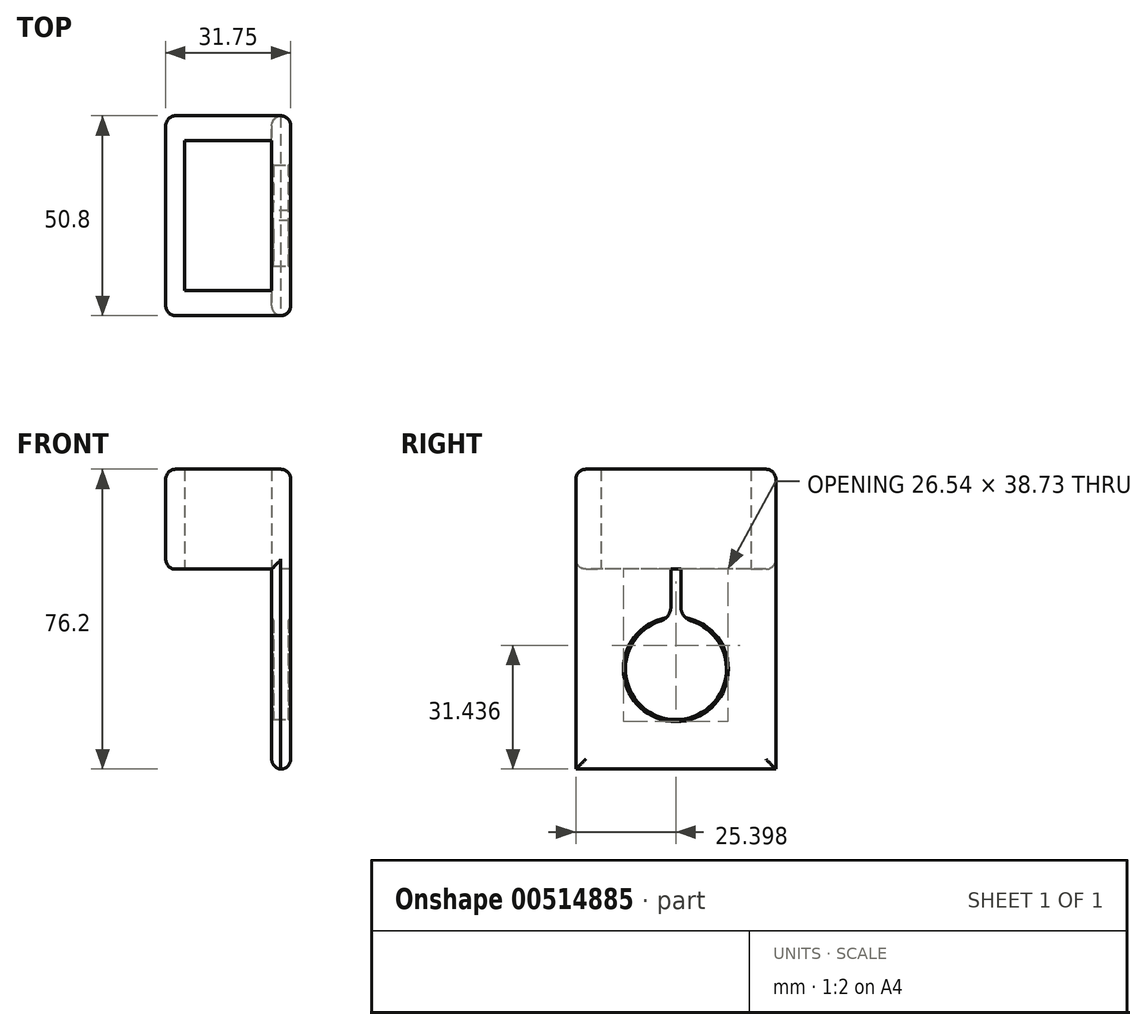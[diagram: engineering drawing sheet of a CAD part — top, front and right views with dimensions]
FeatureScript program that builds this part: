
annotation { "Feature Type Name" : "Feature", "Feature Type Description" : "" }
export const myFeature = defineFeature(function(context is Context, id is Id, definition is map)
    precondition{}
    {
        {
            var Q0;
            Q0=qCreatedBy(makeId("Top.planeOp"),FACE);
            var sketch = newSketch(context, id + "F0", { "sketchPlane" : qUnion([Q0])});
            skLineSegment(sketch, "E0.bottom", {"start": v(0, 0) * mm, "end": v(31.75, 0) * mm});
            skLineSegment(sketch, "E0.top", {"start": v(0, -50.8) * mm, "end": v(31.75, -50.8) * mm});
            skLineSegment(sketch, "E0.left", {"start": v(0, 0) * mm, "end": v(0, -50.8) * mm});
            skLineSegment(sketch, "E0.right", {"start": v(31.75, 0) * mm, "end": v(31.75, -50.8) * mm});
            skLineSegment(sketch, "E1.bottom", {"start": v(4.83, -6.35) * mm, "end": v(26.92, -6.35) * mm});
            skLineSegment(sketch, "E1.top", {"start": v(4.83, -44.45) * mm, "end": v(26.92, -44.45) * mm});
            skLineSegment(sketch, "E1.left", {"start": v(4.83, -6.35) * mm, "end": v(4.83, -44.45) * mm});
            skLineSegment(sketch, "E1.right", {"start": v(26.92, -6.35) * mm, "end": v(26.92, -44.45) * mm});
            skSolve(sketch);
        }
        {
            var Q0;
            Q0=makeQuery(id+"F0.imprint","IMPRINT",FACE,{"disambiguationData":[TD([[makeQuery(id+"F0.imprint","IMPRINT",EDGE,{"derivedFrom":sQuery(id+"F0.wireOp",EDGE,"E0.bottom")}),-1.0]])]});
            extrude(context, id + "F1", {"entities" : qUnion([Q0]), "depth" : 25.4 * mm, "offsetDistance" : 25.4 * mm});
        }
        {
            var Q0;
            Q0=makeQuery(id+"F1.opExtrude","CAP_FACE",FACE,{"disambiguationData":[OSD([sQuery(id+"F0.wireOp",EDGE,"E0.bottom"),sQuery(id+"F0.wireOp",EDGE,"E0.top"),sQuery(id+"F0.wireOp",EDGE,"E0.left"),sQuery(id+"F0.wireOp",EDGE,"E0.right"),sQuery(id+"F0.wireOp",EDGE,"E1.bottom"),sQuery(id+"F0.wireOp",EDGE,"E1.top"),sQuery(id+"F0.wireOp",EDGE,"E1.left"),sQuery(id+"F0.wireOp",EDGE,"E1.right")])],"isStart":true});
            var sketch = newSketch(context, id + "F2", { "sketchPlane" : qUnion([Q0])});
            skPoint(sketch, "E2", {"position": v(26.92, 5.08) * mm});
            skPoint(sketch, "E3", {"position": v(26.92, 6.35) * mm});
            skLineSegment(sketch, "E4", {"start": v(26.92, 5.08) * mm, "end": v(26.92, 6.35) * mm});
            skPoint(sketch, "E5", {"position": v(26.92, 45.72) * mm});
            skLineSegment(sketch, "E6", {"start": v(26.92, 44.45) * mm, "end": v(26.92, 45.72) * mm});
            skLineSegment(sketch, "E7.bottom", {"start": v(26.92, 5.08) * mm, "end": v(31.75, 5.08) * mm});
            skLineSegment(sketch, "E7.left", {"start": v(26.92, 5.08) * mm, "end": v(26.92, 45.72) * mm});
            skLineSegment(sketch, "E7.right", {"start": v(31.75, 5.08) * mm, "end": v(31.75, 45.72) * mm});
            skLineSegment(sketch, "E8", {"start": v(26.92, 5.08) * mm, "end": v(26.92, 0) * mm});
            skLineSegment(sketch, "E9", {"start": v(26.92, 0) * mm, "end": v(31.75, 0) * mm});
            skLineSegment(sketch, "E10", {"start": v(31.75, 0) * mm, "end": v(31.75, 5.08) * mm});
            skLineSegment(sketch, "E11", {"start": v(31.75, 45.72) * mm, "end": v(31.75, 50.8) * mm});
            skLineSegment(sketch, "E12", {"start": v(31.75, 50.8) * mm, "end": v(26.92, 50.8) * mm});
            skLineSegment(sketch, "E13", {"start": v(26.92, 50.8) * mm, "end": v(26.92, 45.72) * mm});
            skSolve(sketch);
        }
        {
            var Q0;
            Q0 = qSketchRegion(id + "F2", true);
            extrude(context, id + "F3", {"entities" : qUnion([Q0]), "operationType" : NewBodyOperationType.ADD, "depth" : 50.8 * mm, "offsetDistance" : 25.4 * mm});
        }
        {
            var Q0;
            Q0=makeQuery(id+"F3.boolean.opBoolean","MERGE",FACE,{"derivedFrom":[makeQuery(id+"F1.opExtrude","SWEPT_FACE",FACE,{"disambiguationData":[OSD([sQuery(id+"F0.wireOp",EDGE,"E1.right")])]}),makeQuery(id+"F3.opExtrude","SWEPT_FACE",FACE,{"disambiguationData":[OSD([sQuery(id+"F2.wireOp",EDGE,"E7.left"),sQuery(id+"F2.wireOp",EDGE,"E8"),sQuery(id+"F2.wireOp",EDGE,"E13")])]})]});
            var sketch = newSketch(context, id + "F4", { "sketchPlane" : qUnion([Q0])});
            skLineSegment(sketch, "E14", {"start": v(0, -25.4) * mm, "end": v(50.8, -25.4) * mm});
            skPoint(sketch, "E15", {"position": v(25.4, -25.4) * mm});
            skCircle(sketch, "E16", {"center": v(25.4, -25.4) * mm, "radius": 12.83 * mm});
            skSolve(sketch);
        }
        {
            var Q0;
            Q0 = qSketchRegion(id + "F4", true);
            extrude(context, id + "F5", {"entities" : qUnion([Q0]), "operationType" : NewBodyOperationType.REMOVE, "depth" : 13.72 * mm, "offsetDistance" : 25.4 * mm, "hasSecondDirection" : true, "secondDirectionOppositeDirection" : true, "secondDirectionDepth" : 25.4 * mm});
        }
        {
            var Q0;
            Q0=makeQuery(id+"F3.opExtrude","SWEPT_EDGE",EDGE,{"disambiguationData":[OSD([sQuery(id+"F2.wireOp",EDGE,"E11"),sQuery(id+"F2.wireOp",EDGE,"E12")])]});
            var Q1;
            Q1=makeQuery(id+"F3.boolean.opBoolean","MERGE",EDGE,{"derivedFrom":[makeQuery(id+"F1.opExtrude","SWEPT_EDGE",EDGE,{"disambiguationData":[OSD([sQuery(id+"F0.wireOp",EDGE,"E0.bottom"),sQuery(id+"F0.wireOp",EDGE,"E0.right")])]}),makeQuery(id+"F3.opExtrude","SWEPT_EDGE",EDGE,{"disambiguationData":[OSD([sQuery(id+"F2.wireOp",EDGE,"E9"),sQuery(id+"F2.wireOp",EDGE,"E10")])]})]});
            var Q2;
            Q2=makeQuery(id+"F1.opExtrude","SWEPT_EDGE",EDGE,{"disambiguationData":[OSD([sQuery(id+"F0.wireOp",EDGE,"E0.bottom"),sQuery(id+"F0.wireOp",EDGE,"E0.left")])]});
            var Q3;
            Q3=makeQuery(id+"F1.opExtrude","SWEPT_EDGE",EDGE,{"disambiguationData":[OSD([sQuery(id+"F0.wireOp",EDGE,"E0.top"),sQuery(id+"F0.wireOp",EDGE,"E0.left")])]});
            var Q4;
            Q4=makeQuery(id+"F1.opExtrude","CAP_EDGE",EDGE,{"disambiguationData":[OSD([sQuery(id+"F0.wireOp",EDGE,"E0.top")])],"isStart":false});
            var Q5;
            Q5=makeQuery(id+"F1.opExtrude","CAP_EDGE",EDGE,{"disambiguationData":[OSD([sQuery(id+"F0.wireOp",EDGE,"E0.right")])],"isStart":false});
            var Q6;
            Q6=makeQuery(id+"F1.opExtrude","CAP_EDGE",EDGE,{"disambiguationData":[OSD([sQuery(id+"F0.wireOp",EDGE,"E0.bottom")])],"isStart":false});
            var Q7;
            Q7=makeQuery(id+"F1.opExtrude","CAP_EDGE",EDGE,{"disambiguationData":[OSD([sQuery(id+"F0.wireOp",EDGE,"E0.left")])],"isStart":true});
            var Q8;
            Q8=makeQuery(id+"F3.boolean.opBoolean","SPLIT",EDGE,{"derivedFrom":makeQuery(id+"F1.opExtrude","CAP_EDGE",EDGE,{"disambiguationData":[OSD([sQuery(id+"F0.wireOp",EDGE,"E0.top")])],"isStart":true})});
            var Q9;
            Q9=makeQuery(id+"F1.opExtrude","CAP_EDGE",EDGE,{"disambiguationData":[OSD([sQuery(id+"F0.wireOp",EDGE,"E0.bottom")])],"isStart":true});
            var Q10;
            Q10=makeQuery(id+"F1.opExtrude","CAP_EDGE",EDGE,{"disambiguationData":[OSD([sQuery(id+"F0.wireOp",EDGE,"E0.left")])],"isStart":false});
            var Q11;
            Q11=makeQuery(id+"F3.opExtrude","CAP_EDGE",EDGE,{"disambiguationData":[OSD([sQuery(id+"F2.wireOp",EDGE,"E7.right"),sQuery(id+"F2.wireOp",EDGE,"E10"),sQuery(id+"F2.wireOp",EDGE,"E11")])],"isStart":false});
            fillet(context, id + "F6", {"entities" : qUnion([Q0, Q1, Q2, Q3, Q4, Q5, Q6, Q7, Q8, Q9, Q10, Q11]), "radius" : 2.54 * mm, "tangentPropagation" : true, "allowEdgeOverflow" : false});
        }
        {
            var Q0;
            Q0=makeQuery(id+"F3.opExtrude","CAP_EDGE",EDGE,{"disambiguationData":[OSD([sQuery(id+"F2.wireOp",EDGE,"E7.left"),sQuery(id+"F2.wireOp",EDGE,"E8"),sQuery(id+"F2.wireOp",EDGE,"E13")])],"isStart":false});
            var Q1;
            Q1=makeQuery(id+"F3.opExtrude","SWEPT_EDGE",EDGE,{"disambiguationData":[OSD([sQuery(id+"F2.wireOp",EDGE,"E12"),sQuery(id+"F2.wireOp",EDGE,"E13")])]});
            var Q2;
            Q2=makeQuery(id+"F3.opExtrude","SWEPT_EDGE",EDGE,{"disambiguationData":[OSD([sQuery(id+"F2.wireOp",EDGE,"E8"),sQuery(id+"F2.wireOp",EDGE,"E9")])]});
            fillet(context, id + "F7", {"entities" : qUnion([Q0, Q1, Q2]), "radius" : 2.54 * mm, "tangentPropagation" : true, "allowEdgeOverflow" : false});
        }
        {
            var Q0;
            Q0=makeQuery(id+"F5.boolean.opBoolean","INTERSECT",EDGE,{"derivedFrom":[makeQuery(id+"F3.boolean.opBoolean","MERGE",FACE,{"derivedFrom":[makeQuery(id+"F1.opExtrude","SWEPT_FACE",FACE,{"disambiguationData":[OSD([sQuery(id+"F0.wireOp",EDGE,"E1.right")])]}),makeQuery(id+"F3.opExtrude","SWEPT_FACE",FACE,{"disambiguationData":[OSD([sQuery(id+"F2.wireOp",EDGE,"E7.left"),sQuery(id+"F2.wireOp",EDGE,"E8"),sQuery(id+"F2.wireOp",EDGE,"E13")])]})]}),makeQuery(id+"F5.opExtrude","SWEPT_FACE",FACE,{"disambiguationData":[OSD([sQuery(id+"F4.wireOp",EDGE,"E16")])]})]});
            var Q1;
            Q1=makeQuery(id+"F5.boolean.opBoolean","INTERSECT",EDGE,{"derivedFrom":[makeQuery(id+"F3.boolean.opBoolean","MERGE",FACE,{"derivedFrom":[makeQuery(id+"F1.opExtrude","SWEPT_FACE",FACE,{"disambiguationData":[OSD([sQuery(id+"F0.wireOp",EDGE,"E0.right")])]}),makeQuery(id+"F3.opExtrude","SWEPT_FACE",FACE,{"disambiguationData":[OSD([sQuery(id+"F2.wireOp",EDGE,"E7.right"),sQuery(id+"F2.wireOp",EDGE,"E10"),sQuery(id+"F2.wireOp",EDGE,"E11")])]})]}),makeQuery(id+"F5.opExtrude","SWEPT_FACE",FACE,{"disambiguationData":[OSD([sQuery(id+"F4.wireOp",EDGE,"E16")])]})]});
            chamfer(context, id + "F8", {"entities" : qUnion([Q0, Q1]), "width" : .5 * mm, "tangentPropagation" : true});
        }
        {
            var Q0;
            Q0=makeQuery(id+"F3.boolean.opBoolean","MERGE",FACE,{"derivedFrom":[makeQuery(id+"F1.opExtrude","SWEPT_FACE",FACE,{"disambiguationData":[OSD([sQuery(id+"F0.wireOp",EDGE,"E1.right")])]}),makeQuery(id+"F3.opExtrude","SWEPT_FACE",FACE,{"disambiguationData":[OSD([sQuery(id+"F2.wireOp",EDGE,"E7.left"),sQuery(id+"F2.wireOp",EDGE,"E8"),sQuery(id+"F2.wireOp",EDGE,"E13")])]})]});
            var sketch = newSketch(context, id + "F9", { "sketchPlane" : qUnion([Q0])});
            skLineSegment(sketch, "E17.bottom", {"start": v(24.13, 0) * mm, "end": v(26.67, 0) * mm});
            skLineSegment(sketch, "E17.top", {"start": v(24.13, -19.05) * mm, "end": v(26.67, -19.05) * mm});
            skLineSegment(sketch, "E17.left", {"start": v(24.13, 0) * mm, "end": v(24.13, -19.05) * mm});
            skLineSegment(sketch, "E17.right", {"start": v(26.67, 0) * mm, "end": v(26.67, -19.05) * mm});
            skPoint(sketch, "E17.middle", {"position": v(25.4, -9.52) * mm});
            skLineSegment(sketch, "E18", {"start": v(25.4, -9.52) * mm, "end": v(25.4, 25.4) * mm, "construction": true});
            skSolve(sketch);
        }
        {
            var Q0;
            Q0 = qSketchRegion(id + "F9", true);
            extrude(context, id + "F10", {"entities" : qUnion([Q0]), "operationType" : NewBodyOperationType.REMOVE, "oppositeDirection" : true, "depth" : 25.4 * mm, "offsetDistance" : 25.4 * mm});
        }
        {
            var Q0;
            Q0=makeQuery(id+"F10.boolean.opBoolean","INTERSECT",EDGE,{"derivedFrom":[makeQuery(id+"F5.boolean.opBoolean","COPY",FACE,{"derivedFrom":makeQuery(id+"F5.opExtrude","SWEPT_FACE",FACE,{"disambiguationData":[OSD([sQuery(id+"F4.wireOp",EDGE,"E16")])]})}),makeQuery(id+"F10.opExtrude","SWEPT_FACE",FACE,{"disambiguationData":[OSD([sQuery(id+"F9.wireOp",EDGE,"E17.right")])]})]});
            var Q1;
            Q1=makeQuery(id+"F10.boolean.opBoolean","INTERSECT",EDGE,{"derivedFrom":[makeQuery(id+"F5.boolean.opBoolean","COPY",FACE,{"derivedFrom":makeQuery(id+"F5.opExtrude","SWEPT_FACE",FACE,{"disambiguationData":[OSD([sQuery(id+"F4.wireOp",EDGE,"E16")])]})}),makeQuery(id+"F10.opExtrude","SWEPT_FACE",FACE,{"disambiguationData":[OSD([sQuery(id+"F9.wireOp",EDGE,"E17.left")])]})]});
            fillet(context, id + "F11", {"entities" : qUnion([Q0, Q1]), "radius" : 3.8 * mm, "tangentPropagation" : true, "allowEdgeOverflow" : false});
        }
    });
